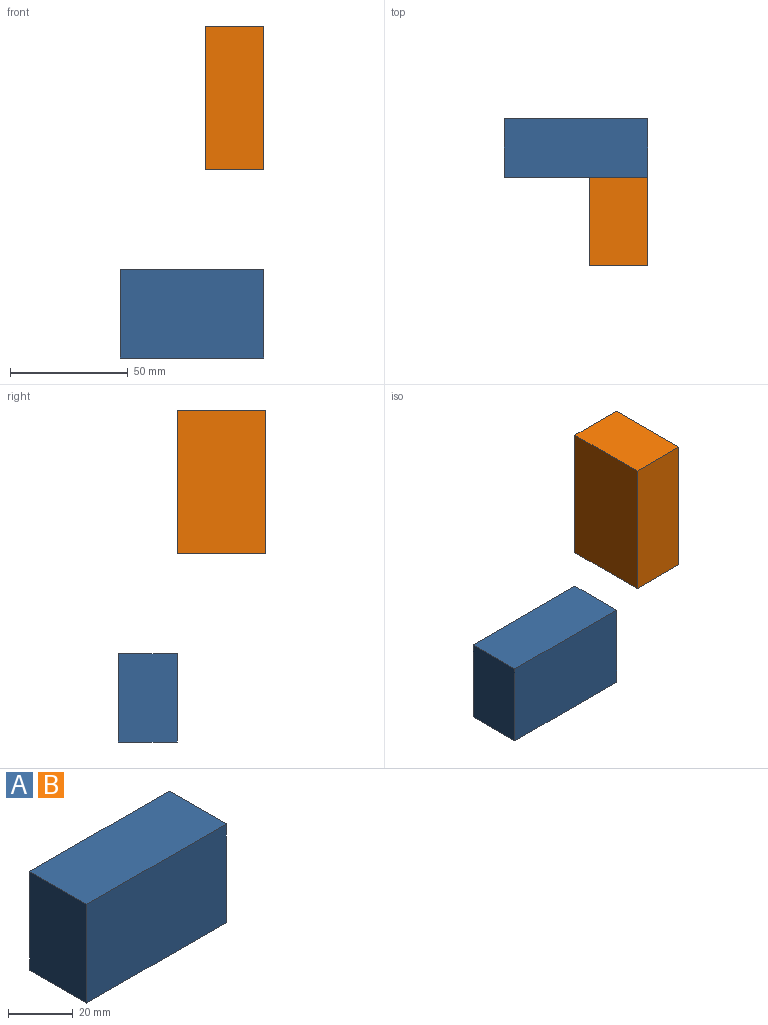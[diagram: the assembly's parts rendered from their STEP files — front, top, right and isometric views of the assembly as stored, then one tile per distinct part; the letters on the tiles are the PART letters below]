
ASSEMBLY  parts=2 mates=1
PART A: 6 faces, bbox 61.1x25x37.4 mm
  f0: plane 61.1x25mm, normal (0,0,1), area 1527.6mm2, adj f1,f3,f4,f5
  f1: plane 37.41x25mm, normal (-1,0,0), area 935.4mm2, adj f0,f2,f4,f5
  f2: plane 61.1x25mm, normal (0,0,-1), area 1527.6mm2, adj f1,f3,f4,f5
  f3: plane 37.41x25mm, normal (1,0,0), area 935.4mm2, adj f0,f2,f4,f5
  f4: plane 61.1x37.41mm, normal (0,-1,0), area 2286.2mm2, adj f0,f1,f2,f3
  f5: plane 61.1x37.41mm, normal (0,1,0), area 2286.2mm2, adj f0,f1,f2,f3
PART B: same geometry as A
PLACE A t=(-57.25,-27.78,-120.65)mm
PLACE B rot(axis=(0.58,0.58,-0.58),120deg) t=(-48.51,-48.78,-28.1)mm
MATE cylindrical B.f3 <-> A.f2  axis (0,0,-1) through (-48.51,-52.78,-36.84)mm
